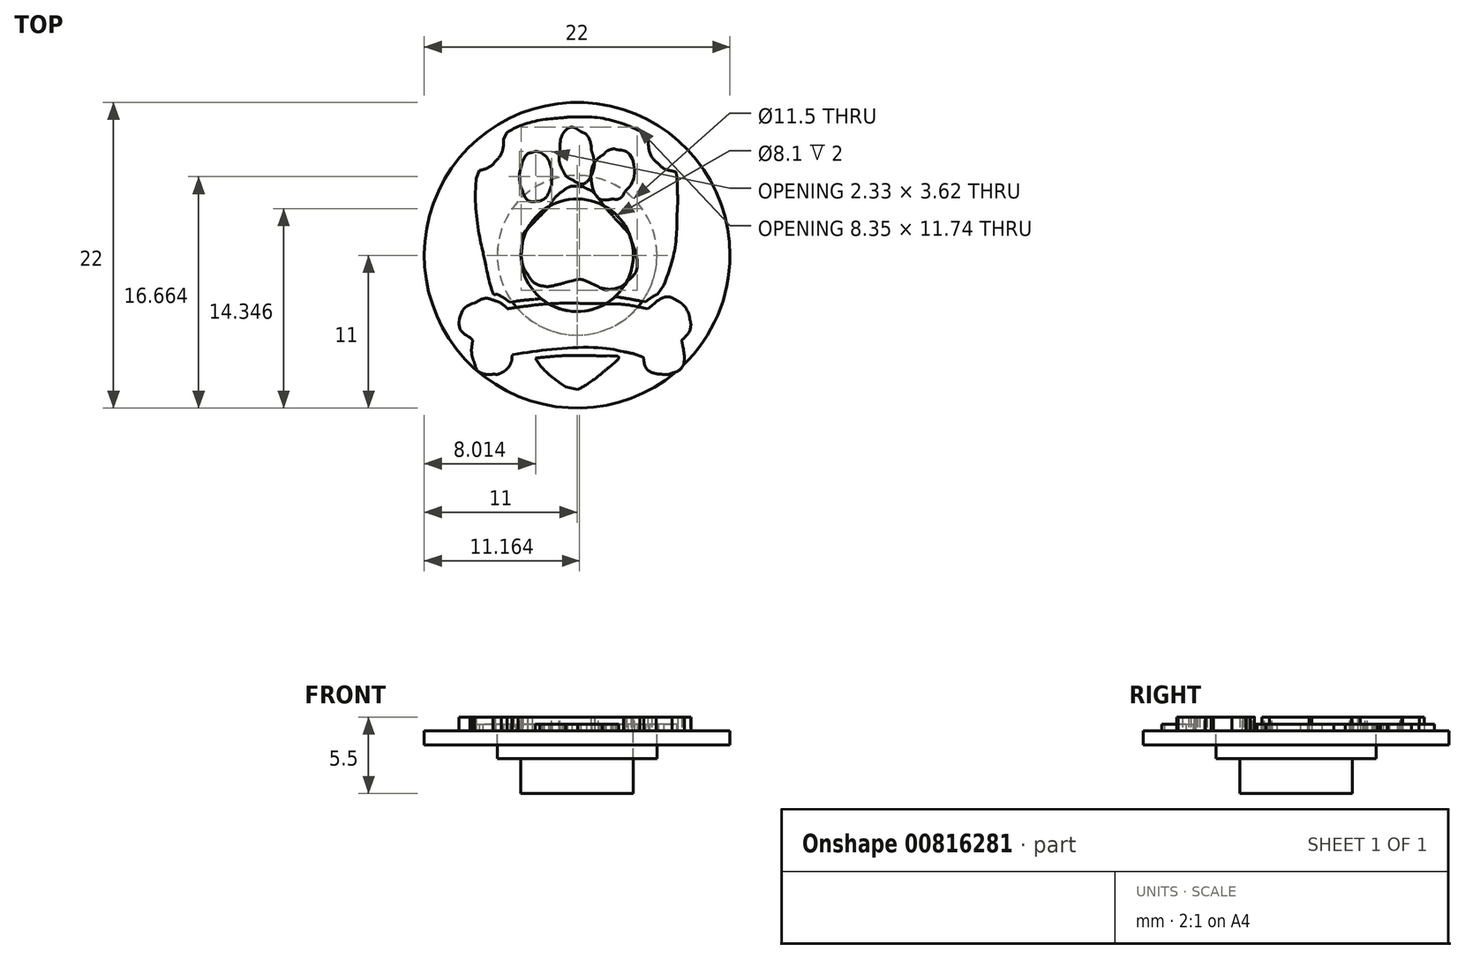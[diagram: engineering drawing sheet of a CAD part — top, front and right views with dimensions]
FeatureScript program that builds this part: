
annotation { "Feature Type Name" : "Feature", "Feature Type Description" : "" }
export const myFeature = defineFeature(function(context is Context, id is Id, definition is map)
    precondition{}
    {
        {
            var Q0;
            Q0=qCreatedBy(makeId("Top.planeOp"),FACE);
            var sketch = newSketch(context, id + "F0", { "sketchPlane" : qUnion([Q0])});
            skCircle(sketch, "E0", {"center": v(0, 0) * mm, "radius": 4.05 * mm});
            skCircle(sketch, "E1", {"center": v(0, 0) * mm, "radius": 5.75 * mm});
            skCircle(sketch, "E2", {"center": v(0, 0) * mm, "radius": 11 * mm});
            skSolve(sketch);
        }
        {
            var Q0;
            Q0=makeQuery(id+"F0.imprint","IMPRINT",FACE,{"disambiguationData":[TD([[makeQuery(id+"F0.imprint","IMPRINT",EDGE,{"derivedFrom":sQuery(id+"F0.wireOp",EDGE,"E0")}),-1.0]])]});
            extrude(context, id + "F1", {"entities" : qUnion([Q0]), "oppositeDirection" : true, "depth" : 2 * mm, "offsetDistance" : 25 * mm});
        }
        {
            var Q0;
            Q0=makeQuery(id+"F0.imprint","IMPRINT",FACE,{"disambiguationData":[TD([[makeQuery(id+"F0.imprint","IMPRINT",EDGE,{"derivedFrom":sQuery(id+"F0.wireOp",EDGE,"E1")}),-1.0]])]});
            extrude(context, id + "F2", {"entities" : qUnion([Q0]), "oppositeDirection" : true, "depth" : 1 * mm, "offsetDistance" : 25 * mm});
        }
        {
            var Q0;
            Q0=makeQuery(id+"F0.imprint","IMPRINT",FACE,{"disambiguationData":[TD([[makeQuery(id+"F0.imprint","IMPRINT",EDGE,{"derivedFrom":sQuery(id+"F0.wireOp",EDGE,"E0")}),1.0]])]});
            extrude(context, id + "F3", {"entities" : qUnion([Q0]), "oppositeDirection" : true, "depth" : 4.5 * mm, "offsetDistance" : 25 * mm});
        }
        {
            var Q0;
            Q0=makeQuery(id+"F3.opExtrude","CAP_FACE",FACE,{"disambiguationData":[OSD([sQuery(id+"F0.wireOp",EDGE,"E0")])],"isStart":true});
            var sketch = newSketch(context, id + "F4", { "sketchPlane" : qUnion([Q0])});
            skLineSegment(sketch, "E3", {"start": v(-5.96, 9.52) * mm, "end": v(-6.36, 9.3) * mm});
            skLineSegment(sketch, "E4", {"start": v(-6.36, 9.3) * mm, "end": v(-6.33, 9.14) * mm});
            skLineSegment(sketch, "E5", {"start": v(-6.33, 9.14) * mm, "end": v(-5.96, 9.52) * mm});
            skLineSegment(sketch, "E6", {"start": v(-7.2, -2.23) * mm, "end": v(-7.03, -2.75) * mm});
            skLineSegment(sketch, "E7", {"start": v(-7.03, -2.75) * mm, "end": v(-6.82, -2.74) * mm});
            skLineSegment(sketch, "E8", {"start": v(-6.82, -2.74) * mm, "end": v(-7.2, -2.23) * mm});
            skLineSegment(sketch, "E9", {"start": v(5.5, 9.16) * mm, "end": v(5.67, 9.07) * mm});
            skLineSegment(sketch, "E10", {"start": v(5.67, 9.07) * mm, "end": v(5.7, 8.55) * mm});
            skLineSegment(sketch, "E11", {"start": v(5.7, 8.55) * mm, "end": v(5.5, 9.16) * mm});
            skLineSegment(sketch, "E12", {"start": v(7.42, 6.59) * mm, "end": v(7.63, 6.61) * mm});
            skLineSegment(sketch, "E13", {"start": v(7.63, 6.61) * mm, "end": v(7.65, 6.45) * mm});
            skLineSegment(sketch, "E14", {"start": v(7.65, 6.45) * mm, "end": v(7.42, 6.59) * mm});
            skLineSegment(sketch, "E15", {"start": v(6.92, -2.7) * mm, "end": v(7.14, -2.73) * mm});
            skLineSegment(sketch, "E16", {"start": v(7.14, -2.73) * mm, "end": v(7.34, -2.11) * mm});
            skLineSegment(sketch, "E17", {"start": v(7.34, -2.11) * mm, "end": v(6.92, -2.7) * mm});
            skLineSegment(sketch, "E18", {"start": v(8.14, 6.33) * mm, "end": v(8.06, 7.1) * mm});
            skLineSegment(sketch, "E19", {"start": v(8.06, 7.1) * mm, "end": v(7.6, 7.07) * mm});
            skLineSegment(sketch, "E20", {"start": v(7.6, 7.07) * mm, "end": v(8.14, 6.33) * mm});
            skLineSegment(sketch, "E21", {"start": v(6.14, 9) * mm, "end": v(6.17, 9.34) * mm});
            skLineSegment(sketch, "E22", {"start": v(6.17, 9.34) * mm, "end": v(5.83, 9.5) * mm});
            skLineSegment(sketch, "E23", {"start": v(5.83, 9.5) * mm, "end": v(6.14, 9) * mm});
            skLineSegment(sketch, "E24", {"start": v(-5.08, 8.82) * mm, "end": v(-5.26, 8.73) * mm});
            skLineSegment(sketch, "E25", {"start": v(-5.26, 8.73) * mm, "end": v(-5.28, 8.34) * mm});
            skLineSegment(sketch, "E26", {"start": v(-5.28, 8.34) * mm, "end": v(-5.08, 8.82) * mm});
            skLineSegment(sketch, "E27", {"start": v(-7.04, 6.1) * mm, "end": v(-7.22, 6.05) * mm});
            skLineSegment(sketch, "E28", {"start": v(-7.22, 6.05) * mm, "end": v(-7.25, 5.52) * mm});
            skLineSegment(sketch, "E29", {"start": v(-7.25, 5.52) * mm, "end": v(-7.04, 6.1) * mm});
            skLineSegment(sketch, "E30", {"start": v(-5.1, -3.2) * mm, "end": v(-4.84, -3.37) * mm});
            skLineSegment(sketch, "E31", {"start": v(-4.84, -3.37) * mm, "end": v(-4.44, -3.31) * mm});
            skLineSegment(sketch, "E32", {"start": v(-4.44, -3.31) * mm, "end": v(-5.1, -3.2) * mm});
            skLineSegment(sketch, "E33", {"start": v(4.48, -3.28) * mm, "end": v(4.92, -3.35) * mm});
            skLineSegment(sketch, "E34", {"start": v(4.92, -3.35) * mm, "end": v(5.22, -3.13) * mm});
            skLineSegment(sketch, "E35", {"start": v(5.22, -3.13) * mm, "end": v(4.48, -3.28) * mm});
            skLineSegment(sketch, "E36", {"start": v(5.78, -2.8) * mm, "end": v(6.04, -2.7) * mm});
            skLineSegment(sketch, "E37", {"start": v(6.04, -2.7) * mm, "end": v(6.24, -2.16) * mm});
            skLineSegment(sketch, "E38", {"start": v(6.24, -2.16) * mm, "end": v(5.78, -2.8) * mm});
            skLineSegment(sketch, "E39", {"start": v(5.13, 8.3) * mm, "end": v(5.1, 8.7) * mm});
            skLineSegment(sketch, "E40", {"start": v(5.1, 8.7) * mm, "end": v(4.77, 8.84) * mm});
            skLineSegment(sketch, "E41", {"start": v(4.77, 8.84) * mm, "end": v(5.13, 8.3) * mm});
            skLineSegment(sketch, "E42", {"start": v(2.43, -2.45) * mm, "end": v(2.08, -2.52) * mm});
            skLineSegment(sketch, "E43", {"start": v(2.08, -2.52) * mm, "end": v(1.64, -2.32) * mm});
            skLineSegment(sketch, "E44", {"start": v(1.64, -2.32) * mm, "end": v(2.43, -2.45) * mm});
            skLineSegment(sketch, "E45", {"start": v(-3.95, -3.54) * mm, "end": v(-4.94, -3.65) * mm});
            skLineSegment(sketch, "E46", {"start": v(-4.94, -3.65) * mm, "end": v(-5.16, -3.47) * mm});
            skLineSegment(sketch, "E47", {"start": v(-5.16, -3.47) * mm, "end": v(-3.95, -3.54) * mm});
            skLineSegment(sketch, "E48", {"start": v(-7.9, -6) * mm, "end": v(-7.74, -6.17) * mm});
            skLineSegment(sketch, "E49", {"start": v(-7.74, -6.17) * mm, "end": v(-7.73, -6.74) * mm});
            skLineSegment(sketch, "E50", {"start": v(-7.73, -6.74) * mm, "end": v(-7.9, -6) * mm});
            skLineSegment(sketch, "E51", {"start": v(4.27, -7.35) * mm, "end": v(4.57, -7.46) * mm});
            skLineSegment(sketch, "E52", {"start": v(4.57, -7.46) * mm, "end": v(4.66, -7.72) * mm});
            skLineSegment(sketch, "E53", {"start": v(4.66, -7.72) * mm, "end": v(4.27, -7.35) * mm});
            skLineSegment(sketch, "E54", {"start": v(7.7, -5.94) * mm, "end": v(7.54, -6.11) * mm});
            skLineSegment(sketch, "E55", {"start": v(7.54, -6.11) * mm, "end": v(7.6, -6.52) * mm});
            skLineSegment(sketch, "E56", {"start": v(7.6, -6.52) * mm, "end": v(7.7, -5.94) * mm});
            skLineSegment(sketch, "E57", {"start": v(-4.23, -7.1) * mm, "end": v(-4.65, -7.14) * mm});
            skLineSegment(sketch, "E58", {"start": v(-4.65, -7.14) * mm, "end": v(-4.68, -7.35) * mm});
            skLineSegment(sketch, "E59", {"start": v(-4.68, -7.35) * mm, "end": v(-4.23, -7.1) * mm});
            skLineSegment(sketch, "E60", {"start": v(-7.55, -6.4) * mm, "end": v(-7.5, -6.1) * mm});
            skLineSegment(sketch, "E61", {"start": v(-7.5, -6.1) * mm, "end": v(-7.71, -5.92) * mm});
            skLineSegment(sketch, "E62", {"start": v(-7.71, -5.92) * mm, "end": v(-7.55, -6.4) * mm});
            skLineSegment(sketch, "E63", {"start": v(4.75, -3.8) * mm, "end": v(5.07, -3.87) * mm});
            skLineSegment(sketch, "E64", {"start": v(5.07, -3.87) * mm, "end": v(5.36, -3.64) * mm});
            skLineSegment(sketch, "E65", {"start": v(5.36, -3.64) * mm, "end": v(4.75, -3.8) * mm});
            skLineSegment(sketch, "E66", {"start": v(-3.01, -7.42) * mm, "end": v(-3.16, -7.45) * mm});
            skLineSegment(sketch, "E67", {"start": v(-3.16, -7.45) * mm, "end": v(-2.7, -7.9) * mm});
            skLineSegment(sketch, "E68", {"start": v(-2.7, -7.9) * mm, "end": v(-3.01, -7.42) * mm});
            skLineSegment(sketch, "E69", {"start": v(-0.83, -9.46) * mm, "end": v(-0.27, -9.84) * mm});
            skLineSegment(sketch, "E70", {"start": v(-0.27, -9.84) * mm, "end": v(0.04, -9.67) * mm});
            skLineSegment(sketch, "E71", {"start": v(0.04, -9.67) * mm, "end": v(-0.83, -9.46) * mm});
            skLineSegment(sketch, "E72", {"start": v(-0.8, -10.7) * mm, "end": v(-0.32, -11) * mm});
            skLineSegment(sketch, "E73", {"start": v(-0.32, -11) * mm, "end": v(0.26, -10.71) * mm});
            skLineSegment(sketch, "E74", {"start": v(0.26, -10.71) * mm, "end": v(-0.8, -10.7) * mm});
            skLineSegment(sketch, "E75", {"start": v(3.93, -7.56) * mm, "end": v(3.7, -7.5) * mm});
            skLineSegment(sketch, "E76", {"start": v(3.7, -7.5) * mm, "end": v(3.44, -7.77) * mm});
            skLineSegment(sketch, "E77", {"start": v(3.44, -7.77) * mm, "end": v(3.93, -7.56) * mm});
            skLineSegment(sketch, "E78", {"start": v(0.14, -10.27) * mm, "end": v(-0.28, -10.49) * mm});
            skLineSegment(sketch, "E79", {"start": v(-0.28, -10.49) * mm, "end": v(-0.42, -10.4) * mm});
            skLineSegment(sketch, "E80", {"start": v(-0.42, -10.4) * mm, "end": v(0.14, -10.27) * mm});
            skFitSpline(sketch, "E81", {"points": [v(-0.9, 10.96) * mm, v(-2.7, 10.81) * mm, v(-4.6, 10.28) * mm, v(-5.96, 9.52) * mm]});
            skFitSpline(sketch, "E82", {"points": [v(-6.33, 9.14) * mm, v(-6.28, 8.87) * mm, v(-6.3, 8.26) * mm, v(-6.38, 8) * mm]});
            skFitSpline(sketch, "E83", {"points": [v(-6.38, 8) * mm, v(-6.42, 7.87) * mm, v(-6.51, 7.67) * mm, v(-6.6, 7.55) * mm]});
            skFitSpline(sketch, "E84", {"points": [v(-6.6, 7.55) * mm, v(-6.82, 7.22) * mm, v(-7.07, 7.12) * mm, v(-7.93, 7.03) * mm]});
            skFitSpline(sketch, "E85", {"points": [v(-7.93, 7.03) * mm, v(-8.18, 7) * mm, v(-8.18, 7) * mm, v(-8.2, 6.84) * mm]});
            skFitSpline(sketch, "E86", {"points": [v(-8.2, 6.84) * mm, v(-8.27, 6.49) * mm, v(-8.29, 4.07) * mm, v(-8.24, 3.34) * mm]});
            skFitSpline(sketch, "E87", {"points": [v(-8.24, 3.34) * mm, v(-8.1, 1.4) * mm, v(-7.73, -0.63) * mm, v(-7.2, -2.23) * mm]});
            skFitSpline(sketch, "E88", {"points": [v(-6.82, -2.74) * mm, v(-6.7, -2.73) * mm, v(-6.6, -2.72) * mm, v(-6.6, -2.7) * mm]});
            skFitSpline(sketch, "E89", {"points": [v(-6.6, -2.7) * mm, v(-6.58, -2.7) * mm, v(-6.68, -2.38) * mm, v(-6.8, -1.99) * mm]});
            skFitSpline(sketch, "E90", {"points": [v(-6.8, -1.99) * mm, v(-7.43, 0.06) * mm, v(-7.75, 2.03) * mm, v(-7.83, 4.37) * mm]});
            skFitSpline(sketch, "E91", {"points": [v(-7.83, 4.37) * mm, v(-7.86, 5.4) * mm, v(-7.81, 6.47) * mm, v(-7.73, 6.55) * mm]});
            skFitSpline(sketch, "E92", {"points": [v(-7.73, 6.55) * mm, v(-7.7, 6.58) * mm, v(-7.54, 6.62) * mm, v(-7.38, 6.63) * mm]});
            skFitSpline(sketch, "E93", {"points": [v(-7.38, 6.63) * mm, v(-6.86, 6.68) * mm, v(-6.38, 6.98) * mm, v(-6.12, 7.43) * mm]});
            skFitSpline(sketch, "E94", {"points": [v(-6.12, 7.43) * mm, v(-5.96, 7.7) * mm, v(-5.84, 8.23) * mm, v(-5.84, 8.7) * mm]});
            skFitSpline(sketch, "E95", {"points": [v(-5.84, 8.7) * mm, v(-5.84, 9) * mm, v(-5.83, 9.1) * mm, v(-5.79, 9.1) * mm]});
            skFitSpline(sketch, "E96", {"points": [v(-5.44, 9.28) * mm, v(-5.06, 9.52) * mm, v(-3.91, 9.94) * mm, v(-3.1, 10.14) * mm]});
            skFitSpline(sketch, "E97", {"points": [v(-3.1, 10.14) * mm, v(-1.2, 10.6) * mm, v(0.4, 10.65) * mm, v(2.05, 10.3) * mm]});
            skFitSpline(sketch, "E98", {"points": [v(2.05, 10.3) * mm, v(3.2, 10.04) * mm, v(4.6, 9.58) * mm, v(5.5, 9.16) * mm]});
            skFitSpline(sketch, "E99", {"points": [v(5.7, 8.55) * mm, v(5.74, 7.6) * mm, v(6.02, 7.04) * mm, v(6.61, 6.74) * mm]});
            skFitSpline(sketch, "E100", {"points": [v(6.61, 6.74) * mm, v(6.83, 6.63) * mm, v(7.2, 6.56) * mm, v(7.42, 6.59) * mm]});
            skFitSpline(sketch, "E101", {"points": [v(7.65, 6.45) * mm, v(7.67, 6.37) * mm, v(7.7, 6.06) * mm, v(7.72, 5.77) * mm]});
            skFitSpline(sketch, "E102", {"points": [v(7.72, 5.77) * mm, v(7.96, 2.82) * mm, v(7.65, 0.1) * mm, v(6.8, -2.3) * mm]});
            skFitSpline(sketch, "E103", {"points": [v(6.8, -2.3) * mm, v(6.74, -2.5) * mm, v(6.68, -2.66) * mm, v(6.69, -2.67) * mm]});
            skFitSpline(sketch, "E104", {"points": [v(6.69, -2.67) * mm, v(6.7, -2.67) * mm, v(6.8, -2.7) * mm, v(6.92, -2.7) * mm]});
            skFitSpline(sketch, "E105", {"points": [v(7.34, -2.11) * mm, v(7.82, -0.66) * mm, v(8.08, 0.68) * mm, v(8.2, 2.36) * mm]});
            skFitSpline(sketch, "E106", {"points": [v(8.2, 2.36) * mm, v(8.27, 3.24) * mm, v(8.24, 5.32) * mm, v(8.14, 6.33) * mm]});
            skFitSpline(sketch, "E107", {"points": [v(7.6, 7.07) * mm, v(7.08, 7.04) * mm, v(6.84, 7.09) * mm, v(6.6, 7.3) * mm]});
            skFitSpline(sketch, "E108", {"points": [v(6.6, 7.3) * mm, v(6.27, 7.58) * mm, v(6.09, 8.26) * mm, v(6.14, 9) * mm]});
            skFitSpline(sketch, "E109", {"points": [v(5.83, 9.5) * mm, v(5.08, 9.87) * mm, v(3.69, 10.36) * mm, v(2.77, 10.6) * mm]});
            skFitSpline(sketch, "E110", {"points": [v(2.77, 10.6) * mm, v(2.08, 10.77) * mm, v(1.21, 10.91) * mm, v(0.57, 10.96) * mm]});
            skFitSpline(sketch, "E111", {"points": [v(0.57, 10.96) * mm, v(-0.1, 11.01) * mm, v(-0.22, 11.01) * mm, v(-0.9, 10.96) * mm]});
            skFitSpline(sketch, "E112", {"points": [v(-0.7, 9.94) * mm, v(-0.74, 9.94) * mm, v(-1, 9.9) * mm, v(-1.26, 9.88) * mm]});
            skFitSpline(sketch, "E113", {"points": [v(-1.26, 9.88) * mm, v(-2.62, 9.73) * mm, v(-4.12, 9.31) * mm, v(-5.08, 8.82) * mm]});
            skFitSpline(sketch, "E114", {"points": [v(-5.28, 8.34) * mm, v(-5.33, 7.73) * mm, v(-5.56, 7.13) * mm, v(-5.92, 6.72) * mm]});
            skFitSpline(sketch, "E115", {"points": [v(-5.92, 6.72) * mm, v(-6.14, 6.47) * mm, v(-6.6, 6.21) * mm, v(-7.04, 6.1) * mm]});
            skFitSpline(sketch, "E116", {"points": [v(-7.25, 5.52) * mm, v(-7.32, 4.2) * mm, v(-7.12, 1.9) * mm, v(-6.8, 0.31) * mm]});
            skFitSpline(sketch, "E117", {"points": [v(-6.8, 0.31) * mm, v(-6.53, -0.95) * mm, v(-5.98, -2.82) * mm, v(-5.86, -2.82) * mm]});
            skFitSpline(sketch, "E118", {"points": [v(-5.86, -2.82) * mm, v(-5.77, -2.82) * mm, v(-5.35, -3.03) * mm, v(-5.1, -3.2) * mm]});
            skFitSpline(sketch, "E119", {"points": [v(-4.44, -3.31) * mm, v(-4.22, -3.28) * mm, v(-3.6, -3.22) * mm, v(-3.06, -3.17) * mm]});
            skFitSpline(sketch, "E120", {"points": [v(-3.06, -3.17) * mm, v(-0.05, -2.9) * mm, v(2.32, -2.93) * mm, v(4.48, -3.28) * mm]});
            skFitSpline(sketch, "E121", {"points": [v(5.22, -3.13) * mm, v(5.4, -3) * mm, v(5.64, -2.87) * mm, v(5.78, -2.8) * mm]});
            skFitSpline(sketch, "E122", {"points": [v(6.24, -2.16) * mm, v(6.78, -0.6) * mm, v(7.12, 1.1) * mm, v(7.18, 2.72) * mm]});
            skFitSpline(sketch, "E123", {"points": [v(7.18, 2.72) * mm, v(7.2, 3.06) * mm, v(7.2, 3.42) * mm, v(7.22, 3.53) * mm]});
            skFitSpline(sketch, "E124", {"points": [v(7.22, 3.53) * mm, v(7.24, 3.78) * mm, v(7.17, 5.68) * mm, v(7.14, 5.86) * mm]});
            skFitSpline(sketch, "E125", {"points": [v(7.14, 5.86) * mm, v(7.11, 5.99) * mm, v(7.1, 6) * mm, v(6.82, 6.07) * mm]});
            skFitSpline(sketch, "E126", {"points": [v(6.82, 6.07) * mm, v(6.4, 6.17) * mm, v(6.1, 6.34) * mm, v(5.84, 6.6) * mm]});
            skFitSpline(sketch, "E127", {"points": [v(5.84, 6.6) * mm, v(5.4, 7.02) * mm, v(5.17, 7.6) * mm, v(5.13, 8.3) * mm]});
            skFitSpline(sketch, "E128", {"points": [v(4.77, 8.84) * mm, v(3.2, 9.5) * mm, v(1.46, 9.9) * mm, v(0.1, 9.94) * mm]});
            skFitSpline(sketch, "E129", {"points": [v(0.1, 9.94) * mm, v(-0.3, 9.95) * mm, v(-0.64, 9.95) * mm, v(-0.7, 9.94) * mm]});
            skFitSpline(sketch, "E130", {"points": [v(0.27, 8.9) * mm, v(0.63, 8.73) * mm, v(0.95, 8.17) * mm, v(1.03, 7.58) * mm]});
            skFitSpline(sketch, "E131", {"points": [v(1.03, 7.58) * mm, v(1.2, 6.26) * mm, v(0.46, 5.14) * mm, v(-0.38, 5.46) * mm]});
            skFitSpline(sketch, "E132", {"points": [v(-0.38, 5.46) * mm, v(-0.6, 5.54) * mm, v(-0.88, 5.82) * mm, v(-1, 6.08) * mm]});
            skFitSpline(sketch, "E133", {"points": [v(-1, 6.08) * mm, v(-1.2, 6.46) * mm, v(-1.3, 7.04) * mm, v(-1.23, 7.5) * mm]});
            skFitSpline(sketch, "E134", {"points": [v(-1.23, 7.5) * mm, v(-1.1, 8.61) * mm, v(-0.43, 9.22) * mm, v(0.27, 8.9) * mm]});
            skFitSpline(sketch, "E135", {"points": [v(2.88, 7.6) * mm, v(3.75, 7.3) * mm, v(4.09, 5.6) * mm, v(3.47, 4.61) * mm]});
            skFitSpline(sketch, "E136", {"points": [v(3.47, 4.61) * mm, v(3.2, 4.2) * mm, v(2.92, 4.03) * mm, v(2.57, 4.06) * mm]});
            skFitSpline(sketch, "E137", {"points": [v(2.57, 4.06) * mm, v(1.48, 4.15) * mm, v(1.07, 6.3) * mm, v(1.94, 7.28) * mm]});
            skFitSpline(sketch, "E138", {"points": [v(1.94, 7.28) * mm, v(2.08, 7.45) * mm, v(2.25, 7.56) * mm, v(2.46, 7.62) * mm]});
            skFitSpline(sketch, "E139", {"points": [v(2.46, 7.62) * mm, v(2.62, 7.67) * mm, v(2.64, 7.67) * mm, v(2.88, 7.6) * mm]});
            skFitSpline(sketch, "E140", {"points": [v(-2.48, 7.28) * mm, v(-2.25, 7.12) * mm, v(-2.05, 6.82) * mm, v(-1.92, 6.46) * mm]});
            skFitSpline(sketch, "E141", {"points": [v(-1.92, 6.46) * mm, v(-1.84, 6.2) * mm, v(-1.82, 6.07) * mm, v(-1.82, 5.64) * mm]});
            skFitSpline(sketch, "E142", {"points": [v(-1.82, 5.64) * mm, v(-1.82, 5.17) * mm, v(-1.83, 5.08) * mm, v(-1.95, 4.78) * mm]});
            skFitSpline(sketch, "E143", {"points": [v(-1.95, 4.78) * mm, v(-2.08, 4.42) * mm, v(-2.35, 4.06) * mm, v(-2.59, 3.94) * mm]});
            skFitSpline(sketch, "E144", {"points": [v(-2.59, 3.94) * mm, v(-2.65, 3.9) * mm, v(-2.82, 3.88) * mm, v(-2.96, 3.88) * mm]});
            skFitSpline(sketch, "E145", {"points": [v(-2.96, 3.88) * mm, v(-3.4, 3.88) * mm, v(-3.75, 4.19) * mm, v(-3.98, 4.79) * mm]});
            skFitSpline(sketch, "E146", {"points": [v(-3.98, 4.79) * mm, v(-4.1, 5.13) * mm, v(-4.14, 5.88) * mm, v(-4.04, 6.26) * mm]});
            skFitSpline(sketch, "E147", {"points": [v(-4.04, 6.26) * mm, v(-3.9, 6.84) * mm, v(-3.56, 7.3) * mm, v(-3.22, 7.4) * mm]});
            skFitSpline(sketch, "E148", {"points": [v(-3.22, 7.4) * mm, v(-3, 7.47) * mm, v(-2.67, 7.42) * mm, v(-2.48, 7.28) * mm]});
            skFitSpline(sketch, "E149", {"points": [v(0.68, 4.8) * mm, v(1.07, 4.6) * mm, v(1.31, 4.39) * mm, v(1.74, 3.82) * mm]});
            skFitSpline(sketch, "E150", {"points": [v(1.74, 3.82) * mm, v(1.94, 3.56) * mm, v(2.4, 3) * mm, v(2.78, 2.6) * mm]});
            skFitSpline(sketch, "E151", {"points": [v(2.78, 2.6) * mm, v(3.67, 1.61) * mm, v(3.74, 1.53) * mm, v(3.87, 1.12) * mm]});
            skFitSpline(sketch, "E152", {"points": [v(3.87, 1.12) * mm, v(4.3, -0.2) * mm, v(4.22, -1.2) * mm, v(3.64, -1.83) * mm]});
            skFitSpline(sketch, "E153", {"points": [v(3.64, -1.83) * mm, v(3.36, -2.13) * mm, v(2.94, -2.35) * mm, v(2.43, -2.45) * mm]});
            skFitSpline(sketch, "E154", {"points": [v(1.64, -2.32) * mm, v(0.47, -1.79) * mm, v(0.1, -1.74) * mm, v(-0.97, -2) * mm]});
            skFitSpline(sketch, "E155", {"points": [v(-0.97, -2) * mm, v(-1.71, -2.2) * mm, v(-2.17, -2.26) * mm, v(-2.37, -2.23) * mm]});
            skFitSpline(sketch, "E156", {"points": [v(-2.37, -2.23) * mm, v(-2.8, -2.14) * mm, v(-3.26, -1.8) * mm, v(-3.54, -1.38) * mm]});
            skFitSpline(sketch, "E157", {"points": [v(-3.54, -1.38) * mm, v(-3.86, -0.88) * mm, v(-4.01, -0.02) * mm, v(-3.93, 0.8) * mm]});
            skFitSpline(sketch, "E158", {"points": [v(-3.93, 0.8) * mm, v(-3.85, 1.6) * mm, v(-3.83, 1.63) * mm, v(-2.93, 2.55) * mm]});
            skFitSpline(sketch, "E159", {"points": [v(-2.93, 2.55) * mm, v(-2.23, 3.27) * mm, v(-1.96, 3.57) * mm, v(-1.8, 3.83) * mm]});
            skFitSpline(sketch, "E160", {"points": [v(-1.8, 3.83) * mm, v(-1.68, 4.04) * mm, v(-1.27, 4.45) * mm, v(-1, 4.64) * mm]});
            skFitSpline(sketch, "E161", {"points": [v(-1, 4.64) * mm, v(-0.65, 4.88) * mm, v(-0.36, 4.97) * mm, v(0.05, 4.96) * mm]});
            skFitSpline(sketch, "E162", {"points": [v(0.05, 4.96) * mm, v(0.34, 4.94) * mm, v(0.44, 4.92) * mm, v(0.68, 4.8) * mm]});
            skFitSpline(sketch, "E163", {"points": [v(6.16, -3) * mm, v(5.9, -3.08) * mm, v(5.58, -3.25) * mm, v(5.29, -3.47) * mm]});
            skFitSpline(sketch, "E164", {"points": [v(5.29, -3.47) * mm, v(5.02, -3.67) * mm, v(5.01, -3.67) * mm, v(4.6, -3.58) * mm]});
            skFitSpline(sketch, "E165", {"points": [v(4.6, -3.58) * mm, v(3.66, -3.38) * mm, v(2.34, -3.3) * mm, v(0.55, -3.3) * mm]});
            skFitSpline(sketch, "E166", {"points": [v(0.55, -3.3) * mm, v(-1.04, -3.3) * mm, v(-2.35, -3.37) * mm, v(-3.95, -3.54) * mm]});
            skFitSpline(sketch, "E167", {"points": [v(-5.16, -3.47) * mm, v(-6, -2.83) * mm, v(-6.98, -2.84) * mm, v(-7.7, -3.49) * mm]});
            skFitSpline(sketch, "E168", {"points": [v(-7.7, -3.49) * mm, v(-8.44, -4.15) * mm, v(-8.53, -5.35) * mm, v(-7.9, -6) * mm]});
            skFitSpline(sketch, "E169", {"points": [v(-7.73, -6.74) * mm, v(-7.72, -7.52) * mm, v(-7.6, -7.89) * mm, v(-7.27, -8.27) * mm]});
            skFitSpline(sketch, "E170", {"points": [v(-7.27, -8.27) * mm, v(-7.06, -8.52) * mm, v(-6.73, -8.67) * mm, v(-6.3, -8.73) * mm]});
            skFitSpline(sketch, "E171", {"points": [v(-6.3, -8.73) * mm, v(-5.73, -8.81) * mm, v(-5.33, -8.7) * mm, v(-4.99, -8.36) * mm]});
            skFitSpline(sketch, "E172", {"points": [v(-4.99, -8.36) * mm, v(-4.8, -8.16) * mm, v(-4.58, -7.78) * mm, v(-4.5, -7.48) * mm]});
            skFitSpline(sketch, "E173", {"points": [v(-4.5, -7.48) * mm, v(-4.44, -7.27) * mm, v(-4.55, -7.3) * mm, v(-3.26, -7.17) * mm]});
            skFitSpline(sketch, "E174", {"points": [v(-3.26, -7.17) * mm, v(-1.27, -6.96) * mm, v(0.75, -6.9) * mm, v(2.1, -7) * mm]});
            skFitSpline(sketch, "E175", {"points": [v(2.1, -7) * mm, v(2.9, -7.05) * mm, v(3.86, -7.21) * mm, v(4.27, -7.35) * mm]});
            skFitSpline(sketch, "E176", {"points": [v(4.66, -7.72) * mm, v(4.83, -8.21) * mm, v(5.1, -8.49) * mm, v(5.57, -8.67) * mm]});
            skFitSpline(sketch, "E177", {"points": [v(5.57, -8.67) * mm, v(5.74, -8.73) * mm, v(5.9, -8.75) * mm, v(6.24, -8.75) * mm]});
            skFitSpline(sketch, "E178", {"points": [v(6.24, -8.75) * mm, v(6.67, -8.75) * mm, v(6.72, -8.74) * mm, v(6.96, -8.61) * mm]});
            skFitSpline(sketch, "E179", {"points": [v(6.96, -8.61) * mm, v(7.65, -8.26) * mm, v(7.92, -7.5) * mm, v(7.77, -6.43) * mm]});
            skFitSpline(sketch, "E180", {"points": [v(7.77, -6.43) * mm, v(7.74, -6.2) * mm, v(7.74, -6.18) * mm, v(7.88, -6.01) * mm]});
            skFitSpline(sketch, "E181", {"points": [v(7.88, -6.01) * mm, v(8.08, -5.79) * mm, v(8.24, -5.43) * mm, v(8.3, -5.12) * mm]});
            skFitSpline(sketch, "E182", {"points": [v(8.3, -5.12) * mm, v(8.38, -4.66) * mm, v(8.2, -4.02) * mm, v(7.84, -3.54) * mm]});
            skFitSpline(sketch, "E183", {"points": [v(7.84, -3.54) * mm, v(7.48, -3.08) * mm, v(6.75, -2.84) * mm, v(6.16, -3) * mm]});
            skFitSpline(sketch, "E184", {"points": [v(7.23, -3.3) * mm, v(7.38, -3.37) * mm, v(7.56, -3.5) * mm, v(7.64, -3.59) * mm]});
            skFitSpline(sketch, "E185", {"points": [v(7.64, -3.59) * mm, v(7.83, -3.8) * mm, v(8.06, -4.31) * mm, v(8.11, -4.62) * mm]});
            skFitSpline(sketch, "E186", {"points": [v(8.11, -4.62) * mm, v(8.18, -5.06) * mm, v(8.02, -5.59) * mm, v(7.7, -5.94) * mm]});
            skFitSpline(sketch, "E187", {"points": [v(7.6, -6.52) * mm, v(7.71, -7.51) * mm, v(7.45, -8.2) * mm, v(6.84, -8.47) * mm]});
            skFitSpline(sketch, "E188", {"points": [v(6.84, -8.47) * mm, v(6.66, -8.56) * mm, v(6.54, -8.57) * mm, v(6.24, -8.57) * mm]});
            skFitSpline(sketch, "E189", {"points": [v(6.24, -8.57) * mm, v(6.04, -8.57) * mm, v(5.8, -8.55) * mm, v(5.7, -8.52) * mm]});
            skFitSpline(sketch, "E190", {"points": [v(5.7, -8.52) * mm, v(5.26, -8.4) * mm, v(4.9, -8.03) * mm, v(4.8, -7.57) * mm]});
            skFitSpline(sketch, "E191", {"points": [v(4.8, -7.57) * mm, v(4.75, -7.34) * mm, v(4.75, -7.34) * mm, v(4.52, -7.26) * mm]});
            skFitSpline(sketch, "E192", {"points": [v(4.52, -7.26) * mm, v(4.25, -7.15) * mm, v(3.73, -7.02) * mm, v(3.34, -6.95) * mm]});
            skFitSpline(sketch, "E193", {"points": [v(3.34, -6.95) * mm, v(1.78, -6.67) * mm, v(-1.34, -6.73) * mm, v(-4.23, -7.1) * mm]});
            skFitSpline(sketch, "E194", {"points": [v(-4.68, -7.35) * mm, v(-4.71, -7.61) * mm, v(-4.88, -7.97) * mm, v(-5.06, -8.18) * mm]});
            skFitSpline(sketch, "E195", {"points": [v(-5.06, -8.18) * mm, v(-5.13, -8.27) * mm, v(-5.3, -8.4) * mm, v(-5.44, -8.46) * mm]});
            skFitSpline(sketch, "E196", {"points": [v(-5.44, -8.46) * mm, v(-5.66, -8.56) * mm, v(-5.73, -8.57) * mm, v(-6.04, -8.57) * mm]});
            skFitSpline(sketch, "E197", {"points": [v(-6.04, -8.57) * mm, v(-6.72, -8.55) * mm, v(-7.2, -8.25) * mm, v(-7.4, -7.72) * mm]});
            skFitSpline(sketch, "E198", {"points": [v(-7.4, -7.72) * mm, v(-7.53, -7.37) * mm, v(-7.6, -6.77) * mm, v(-7.55, -6.4) * mm]});
            skFitSpline(sketch, "E199", {"points": [v(-7.71, -5.92) * mm, v(-8.43, -5.27) * mm, v(-8.2, -3.92) * mm, v(-7.26, -3.39) * mm]});
            skFitSpline(sketch, "E200", {"points": [v(-7.26, -3.39) * mm, v(-6.85, -3.15) * mm, v(-6.38, -3.12) * mm, v(-5.9, -3.28) * mm]});
            skFitSpline(sketch, "E201", {"points": [v(-5.9, -3.28) * mm, v(-5.68, -3.35) * mm, v(-5.28, -3.6) * mm, v(-5.1, -3.75) * mm]});
            skFitSpline(sketch, "E202", {"points": [v(-5.1, -3.75) * mm, v(-5, -3.85) * mm, v(-5, -3.85) * mm, v(-4.56, -3.8) * mm]});
            skFitSpline(sketch, "E203", {"points": [v(-4.56, -3.8) * mm, v(-2.8, -3.56) * mm, v(-0.91, -3.45) * mm, v(1.05, -3.48) * mm]});
            skFitSpline(sketch, "E204", {"points": [v(1.05, -3.48) * mm, v(2.82, -3.5) * mm, v(3.7, -3.58) * mm, v(4.75, -3.8) * mm]});
            skFitSpline(sketch, "E205", {"points": [v(5.36, -3.64) * mm, v(6.06, -3.1) * mm, v(6.63, -3) * mm, v(7.23, -3.3) * mm]});
            skFitSpline(sketch, "E206", {"points": [v(-1.06, -7.23) * mm, v(-1.64, -7.27) * mm, v(-2.88, -7.4) * mm, v(-3.01, -7.42) * mm]});
            skFitSpline(sketch, "E207", {"points": [v(-2.7, -7.9) * mm, v(-2.12, -8.5) * mm, v(-1.52, -9) * mm, v(-0.83, -9.46) * mm]});
            skFitSpline(sketch, "E208", {"points": [v(0.04, -9.67) * mm, v(0.55, -9.4) * mm, v(1.29, -8.9) * mm, v(1.81, -8.46) * mm]});
            skFitSpline(sketch, "E209", {"points": [v(1.81, -8.46) * mm, v(2.32, -8.05) * mm, v(2.98, -7.44) * mm, v(2.98, -7.39) * mm]});
            skFitSpline(sketch, "E210", {"points": [v(2.98, -7.39) * mm, v(2.98, -7.3) * mm, v(1.94, -7.24) * mm, v(0.61, -7.23) * mm]});
            skFitSpline(sketch, "E211", {"points": [v(0.61, -7.23) * mm, v(-0.17, -7.23) * mm, v(-0.93, -7.23) * mm, v(-1.06, -7.23) * mm]});
            skFitSpline(sketch, "E212", {"points": [v(-4.07, -7.54) * mm, v(-4.12, -7.56) * mm, v(-4.17, -7.61) * mm, v(-4.2, -7.67) * mm]});
            skFitSpline(sketch, "E213", {"points": [v(-4.2, -7.67) * mm, v(-4.23, -7.77) * mm, v(-4.2, -7.81) * mm, v(-3.98, -8.07) * mm]});
            skFitSpline(sketch, "E214", {"points": [v(-3.98, -8.07) * mm, v(-3.07, -9.1) * mm, v(-1.97, -10) * mm, v(-0.8, -10.7) * mm]});
            skFitSpline(sketch, "E215", {"points": [v(0.26, -10.71) * mm, v(1.15, -10.27) * mm, v(2.25, -9.5) * mm, v(3.08, -8.74) * mm]});
            skFitSpline(sketch, "E216", {"points": [v(3.08, -8.74) * mm, v(3.46, -8.4) * mm, v(4.16, -7.68) * mm, v(4.16, -7.63) * mm]});
            skFitSpline(sketch, "E217", {"points": [v(4.16, -7.63) * mm, v(4.16, -7.62) * mm, v(4.05, -7.58) * mm, v(3.93, -7.56) * mm]});
            skFitSpline(sketch, "E218", {"points": [v(3.44, -7.77) * mm, v(3.14, -8.1) * mm, v(2.3, -8.83) * mm, v(1.9, -9.14) * mm]});
            skFitSpline(sketch, "E219", {"points": [v(1.9, -9.14) * mm, v(1.41, -9.51) * mm, v(0.57, -10.06) * mm, v(0.14, -10.27) * mm]});
            skFitSpline(sketch, "E220", {"points": [v(-0.42, -10.4) * mm, v(-1.46, -9.8) * mm, v(-2.52, -8.96) * mm, v(-3.43, -7.98) * mm]});
            skFitSpline(sketch, "E221", {"points": [v(-3.43, -7.98) * mm, v(-3.85, -7.53) * mm, v(-3.9, -7.5) * mm, v(-4.07, -7.54) * mm]});
            skLineSegment(sketch, "E222", {"start": v(-5.79, 9.1) * mm, "end": v(-5.44, 9.28) * mm});
            skSolve(sketch);
        }
        {
            var Q0;
            {var subQ5=sQuery(id+"F4.wireOp",EDGE,"E149");Q0=makeQuery(id+"F4.imprint","IMPRINT",FACE,{"disambiguationData":[TD([[makeQuery(id+"F4.imprint","IMPRINT",EDGE,{"derivedFrom":subQ5}),-1.0]])]});}
            var Q1;
            {var subQ5=sQuery(id+"F4.wireOp",EDGE,"E44");Q1=makeQuery(id+"F4.imprint","IMPRINT",FACE,{"disambiguationData":[TD([[makeQuery(id+"F4.imprint","IMPRINT",EDGE,{"derivedFrom":subQ5}),1.0]])]});}
            var Q2;
            Q2=makeQuery(id+"F4.imprint","IMPRINT",FACE,{"disambiguationData":[TD([[makeQuery(id+"F4.imprint","IMPRINT",EDGE,{"derivedFrom":sQuery(id+"F4.wireOp",EDGE,"E130")}),-1.0]])]});
            var Q3;
            Q3=makeQuery(id+"F4.imprint","IMPRINT",FACE,{"disambiguationData":[TD([[makeQuery(id+"F4.imprint","IMPRINT",EDGE,{"derivedFrom":sQuery(id+"F4.wireOp",EDGE,"E140")}),-1.0]])]});
            var Q4;
            Q4=makeQuery(id+"F4.imprint","IMPRINT",FACE,{"disambiguationData":[TD([[makeQuery(id+"F4.imprint","IMPRINT",EDGE,{"derivedFrom":sQuery(id+"F4.wireOp",EDGE,"E135")}),-1.0]])]});
            var Q5;
            Q5=makeQuery(id+"F4.imprint","IMPRINT",FACE,{"disambiguationData":[TD([[makeQuery(id+"F4.imprint","IMPRINT",EDGE,{"derivedFrom":sQuery(id+"F4.wireOp",EDGE,"E54")}),-1.0]])]});
            extrude(context, id + "F5", {"entities" : qUnion([Q0, Q1, Q2, Q3, Q4, Q5]), "depth" : 1 * mm, "offsetDistance" : 25 * mm});
        }
        {
            var Q0;
            Q0=makeQuery(id+"F4.imprint","IMPRINT",FACE,{"disambiguationData":[TD([[makeQuery(id+"F4.imprint","IMPRINT",EDGE,{"derivedFrom":sQuery(id+"F4.wireOp",EDGE,"E26")}),-1.0]])]});
            var Q1;
            Q1=makeQuery(id+"F4.imprint","IMPRINT",FACE,{"disambiguationData":[TD([[makeQuery(id+"F4.imprint","IMPRINT",EDGE,{"derivedFrom":sQuery(id+"F4.wireOp",EDGE,"E68")}),-1.0]])]});
            var Q2;
            {var subQ7=sQuery(id+"F4.wireOp",EDGE,"E42");Q2=makeQuery(id+"F4.imprint","IMPRINT",FACE,{"disambiguationData":[TD([[makeQuery(id+"F4.imprint","IMPRINT",EDGE,{"derivedFrom":subQ7}),1.0]])]});}
            var Q3;
            {var subQ3=makeQuery(id+"F3.opExtrude","CAP_EDGE",EDGE,{"disambiguationData":[OSD([sQuery(id+"F0.wireOp",EDGE,"E0")])],"isStart":true});var subQ5=sQuery(id+"F4.wireOp",EDGE,"E120");var subQ6=makeQuery(id+"F4.imprint","INTERSECT",VERTEX,{"disambiguationData":[OD(0.0)],"derivedFrom":[subQ3,subQ5]});Q3=makeQuery(id+"F4.imprint","IMPRINT",FACE,{"disambiguationData":[TD([[makeQuery(id+"F4.imprint","IMPRINT",EDGE,{"disambiguationData":[TD([[subQ6,-1.0]])],"derivedFrom":subQ5}),-1.0]])]});}
            var Q4;
            {var subQ5=sQuery(id+"F4.wireOp",EDGE,"E166");var subQ6=sQuery(id+"F4.wireOp",EDGE,"E165");var subQ7=makeQuery(id+"F4.imprint","INTERSECT",VERTEX,{"derivedFrom":[subQ6,subQ5]});Q4=makeQuery(id+"F4.imprint","IMPRINT",FACE,{"disambiguationData":[TD([[makeQuery(id+"F4.imprint","IMPRINT",EDGE,{"disambiguationData":[TD([[subQ7,1.0]])],"derivedFrom":subQ6}),1.0]])]});}
            var Q5;
            Q5=makeQuery(id+"F4.imprint","IMPRINT",FACE,{"disambiguationData":[TD([[makeQuery(id+"F4.imprint","IMPRINT",EDGE,{"derivedFrom":sQuery(id+"F4.wireOp",EDGE,"E30")}),1.0]])]});
            var Q6;
            Q6=makeQuery(id+"F4.imprint","IMPRINT",FACE,{"disambiguationData":[TD([[makeQuery(id+"F4.imprint","IMPRINT",EDGE,{"derivedFrom":sQuery(id+"F4.wireOp",EDGE,"E33")}),1.0]])]});
            extrude(context, id + "F6", {"entities" : qUnion([Q0, Q1, Q2, Q3, Q4, Q5, Q6]), "depth" : 0.5 * mm, "offsetDistance" : 25 * mm});
        }
    });
